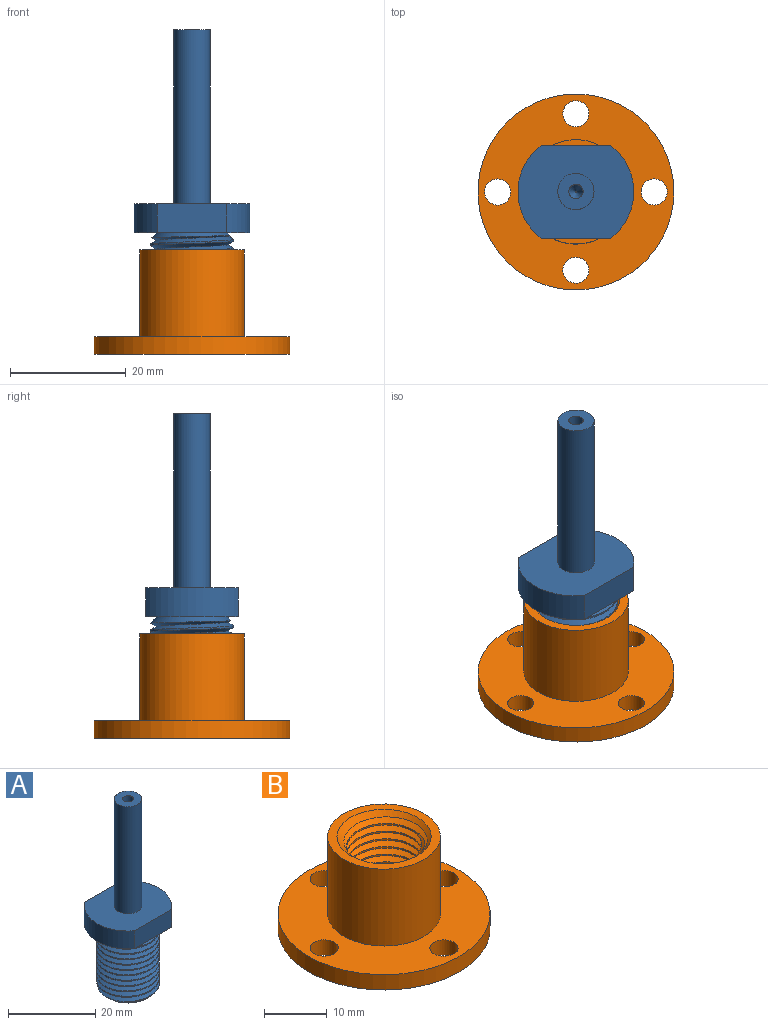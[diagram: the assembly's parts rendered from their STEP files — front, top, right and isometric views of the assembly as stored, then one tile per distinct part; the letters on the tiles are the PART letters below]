
ASSEMBLY  parts=2 mates=1
PART A: 22 faces, bbox 20x16.6x53.5 mm
  f0: plane 20x16mm, normal (0,0,1), area 250.8mm2, adj f2,f17,f18,f19,f20
  f1: plane 20x16mm, normal (0,0,-1), area 168.4mm2, adj f2,f5,f17,f18,f19
  f2: cylinder r=10mm len=16mm, axis (0,0,-1), area 92.7mm2, adj f0,f1,f18,f19
  f3: plane 6x6mm, normal (0,0,-1), area 28.3mm2, adj f13,f14
  f4: cylinder r=7.2mm len=15.6mm, axis (0,0,-1), area 94.6mm2, adj f5,f7,f9,f10
  f5: cone r=6mm half-angle=45deg, axis (0,0,-1), area 51.6mm2, adj f1,f4,f8,f9
  f6: plane 12x12mm, normal (0,0,-1), area 49.5mm2, adj f7,f15
  f7: cone r=7.2mm half-angle=45deg, axis (0,0,1), area 45mm2, adj f4,f6,f9,f10
  f8: plane 1.04x0.76mm, normal (0,-1,0), area 0.2mm2, adj f5,f9,f10
  f9: bspline ~17.85x16.63mm, area 557.3mm2, adj f4,f5,f7,f8,f10
  f10: bspline ~17.85x16.63mm, area 542.8mm2, adj f4,f7,f8,f9
  f11: cylinder r=1.25mm len=50mm, axis (0,0,1), area 392.7mm2, adj f12,f21
  f12: plane 3.56x3.56mm, normal (0,0,-1), area 5.1mm2, adj f11,f13
  f13: cone r=0.05mm half-angle=30deg, axis (0,0,1), area 19.9mm2, adj f3,f12
  f14: cylinder r=3mm len=6mm, axis (0,0,-1), area 22.6mm2, adj f3,f16
  f15: cylinder r=4.5mm len=9mm, axis (0,0,-1), area 33.9mm2, adj f6,f16
  f16: plane 9x9mm, normal (0,0,-1), area 35.3mm2, adj f14,f15
  f17: cylinder r=10mm len=16mm, axis (0,0,-1), area 92.7mm2, adj f0,f1,f18,f19
  f18: plane 12x5mm, normal (0,1,0), area 60mm2, adj f0,f1,f2,f17
  f19: plane 12x5mm, normal (0,-1,0), area 60mm2, adj f0,f1,f2,f17
  f20: cylinder r=3.12mm len=30mm, axis (0,0,-1), area 589mm2, adj f0,f21
  f21: plane 6.25x6.25mm, normal (0,0,1), area 25.8mm2, adj f11,f20
PART B: 16 faces, bbox 33.8x33.8x18.2 mm
  f0: plane 12x12mm, normal (0,0,1), area 110mm2, adj f8,f9
  f1: cylinder r=2.25mm len=4.5mm, axis (0,0,1), area 42.4mm2, adj f5,f6
  f2: cylinder r=2.25mm len=4.5mm, axis (0,0,1), area 42.4mm2, adj f5,f6
  f3: cylinder r=2.25mm len=4.5mm, axis (0,0,1), area 42.4mm2, adj f5,f6
  f4: cylinder r=16.9mm len=33.8mm, axis (0,0,-1), area 318.6mm2, adj f5,f6
  f5: plane 33.8x33.8mm, normal (0,0,1), area 579.2mm2, adj f1,f2,f3,f4,f7,f10
  f6: plane 33.8x33.8mm, normal (0,0,-1), area 713mm2, adj f1,f2,f3,f4,f7,f8
  f7: cylinder r=2.25mm len=4.5mm, axis (0,0,1), area 42.4mm2, adj f5,f6
  f8: cone r=1mm half-angle=60deg, axis (0,0,-1), area 135.6mm2, adj f0,f6
  f9: cylinder r=6mm len=13.5mm, axis (0,0,-1), area 121.5mm2, adj f0,f12,f13,f14,f15
  f10: cylinder r=9mm len=18mm, axis (0,0,-1), area 848.2mm2, adj f5,f11
  f11: plane 18x18mm, normal (0,0,1), area 77.8mm2, adj f10,f12
  f12: cone r=6mm half-angle=45deg, axis (0,0,1), area 66.6mm2, adj f9,f11,f14,f15
  f13: plane 1.2x1.04mm, normal (0,-1,0), area 0.6mm2, adj f9,f14,f15
  f14: bspline ~16.26x14.6mm, area 451.7mm2, adj f9,f12,f13,f15
  f15: bspline ~16.26x14.6mm, area 427.4mm2, adj f9,f12,f13,f14
PLACE A t=(-31.86,1.23,8.57)mm
PLACE B t=(-31.86,1.23,5.57)mm
MATE planar B.f9 <-> A.f14  axis (0,0,1) through (-31.86,1.23,8.57)mm
